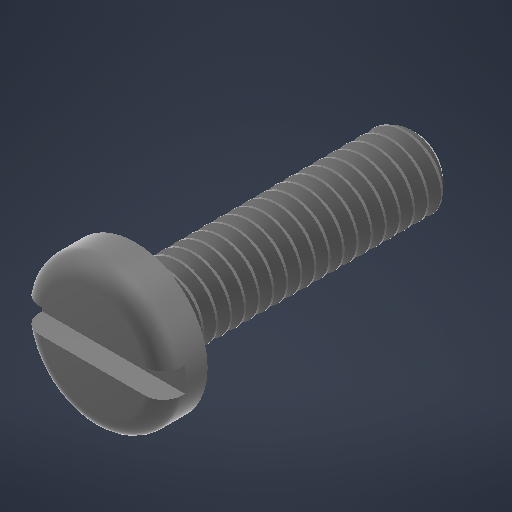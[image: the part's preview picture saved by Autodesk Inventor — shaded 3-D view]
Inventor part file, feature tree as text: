
AUTODESK INVENTOR PART (.ipt)
format: ipt  version: 2025.2 (Build 292293000, 293)  size: 499,712 bytes
history: native  units: in
note: dims shown in document units (in); Inventor stores cm internally (conversion verified against a paired STEP export)
features: other x1, extrude x1
ambient origin geometry x8: Origin, YZ Plane, XZ Plane, XY Plane, X Axis, Y Axis, Z Axis, Center Point
bodies: Solid1 (feature_tree)
feature tree (2):
  other  "Plane1"
  extrude  "Extrude15"  [1 undecoded]
note: 1 required parameter value undecoded (feature->parameter linkage not recoverable at this tier; creation-order binding heuristic only, values carry confidence <= 0.55)
